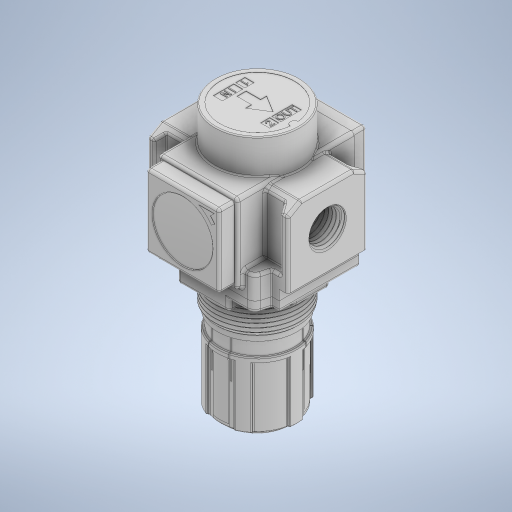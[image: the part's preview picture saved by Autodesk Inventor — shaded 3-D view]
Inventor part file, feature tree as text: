
AUTODESK INVENTOR PART (.ipt)
format: ipt  version: 2024.1 (Build 281209000, 209)  size: 4,400,128 bytes
history: native  units: in
note: dims shown in document units (in); Inventor stores cm internally (conversion verified against a paired STEP export)
features: other x43, sketch x5, fillet x3
ambient origin geometry x8: Origin, YZ Plane, XZ Plane, XY Plane, X Axis, Y Axis, Z Axis, Center Point
bodies: Solid1 (feature_tree), Solid2 (feature_tree), Solid3 (feature_tree), Solid4 (feature_tree), Solid5 (feature_tree), Solid6 (feature_tree), Solid7 (feature_tree), Solid8 (feature_tree), Solid9 (feature_tree), Solid10 (feature_tree), Solid11 (feature_tree), Solid12 (feature_tree), Solid13 (feature_tree), Solid14 (feature_tree), Solid15 (feature_tree), Solid16 (feature_tree), Solid17 (feature_tree), Solid18 (feature_tree), Solid19 (feature_tree), Solid20 (feature_tree), Solid21 (feature_tree), Solid22 (feature_tree), Solid23 (feature_tree), Solid24 (feature_tree), Solid25 (feature_tree), Solid26 (feature_tree), Solid27 (feature_tree), Solid28 (feature_tree), Solid29 (feature_tree), Solid30 (feature_tree), Solid31 (feature_tree), Solid32 (feature_tree), Solid33 (feature_tree), Solid34 (feature_tree), Solid35 (feature_tree), Solid36 (feature_tree), Solid37 (feature_tree), Solid38 (feature_tree), Solid39 (feature_tree), Solid40 (feature_tree), Solid41 (feature_tree), Solid42 (feature_tree), Solid43 (feature_tree), Solid44 (feature_tree), Solid45 (feature_tree), Solid46 (feature_tree), Solid47 (feature_tree), Solid48 (feature_tree), Solid49 (feature_tree), Solid50 (feature_tree), Solid51 (feature_tree)
feature tree (51):
  fillet  "Fillet27"  [1 undecoded]
  fillet  "Fillet21"  [1 undecoded]
  other  "Boss-Extrude9"
  other  "Draft1"
  sketch  "Sketch-Pattern1[1]"
  sketch  "Sketch-Pattern1[2]"
  other  "Draft2"
  sketch  "Sketch-Pattern2[1]"
  sketch  "Sketch-Pattern2[2]"
  sketch  "Sketch-Pattern2[3]"
  other  "Cut-Extrude8"
  other  "Boss-Extrude12"
  fillet  "Fillet19"  [1 undecoded]
  other  "Boss-Extrude14"
  other  "Cut-Extrude9[1]"
  other  "Cut-Extrude9[2]"
  other  "Cut-Extrude11"
  other  "Boss-Extrude17"
  other  "Boss-Extrude18"
  other  "Boss-Extrude19"
  other  "Boss-Extrude20[1]"
  other  "Boss-Extrude20[2]"
  other  "Boss-Extrude20[3]"
  other  "Boss-Extrude20[4]"
  other  "Boss-Extrude20[5]"
  other  "Boss-Extrude20[6]"
  other  "Boss-Extrude20[7]"
  other  "Boss-Extrude20[8]"
  other  "Boss-Extrude20[9]"
  other  "Boss-Extrude20[10]"
  other  "Boss-Extrude20[11]"
  other  "Boss-Extrude20[12]"
  other  "Boss-Extrude20[13]"
  other  "Boss-Extrude20[14]"
  other  "Boss-Extrude20[15]"
  other  "Boss-Extrude20[16]"
  other  "Boss-Extrude20[17]"
  other  "Boss-Extrude20[18]"
  other  "Boss-Extrude20[19]"
  other  "Boss-Extrude20[20]"
  other  "Boss-Extrude20[21]"
  other  "Boss-Extrude20[22]"
  other  "Boss-Extrude20[23]"
  other  "Boss-Extrude20[24]"
  other  "Boss-Extrude20[25]"
  other  "Boss-Extrude20[26]"
  other  "Boss-Extrude20[27]"
  other  "Boss-Extrude20[28]"
  other  "Boss-Extrude20[29]"
  other  "Boss-Extrude20[30]"
  other  "Boss-Extrude20[31]"
note: 3 required parameter values undecoded (feature->parameter linkage not recoverable at this tier; creation-order binding heuristic only, values carry confidence <= 0.55)
